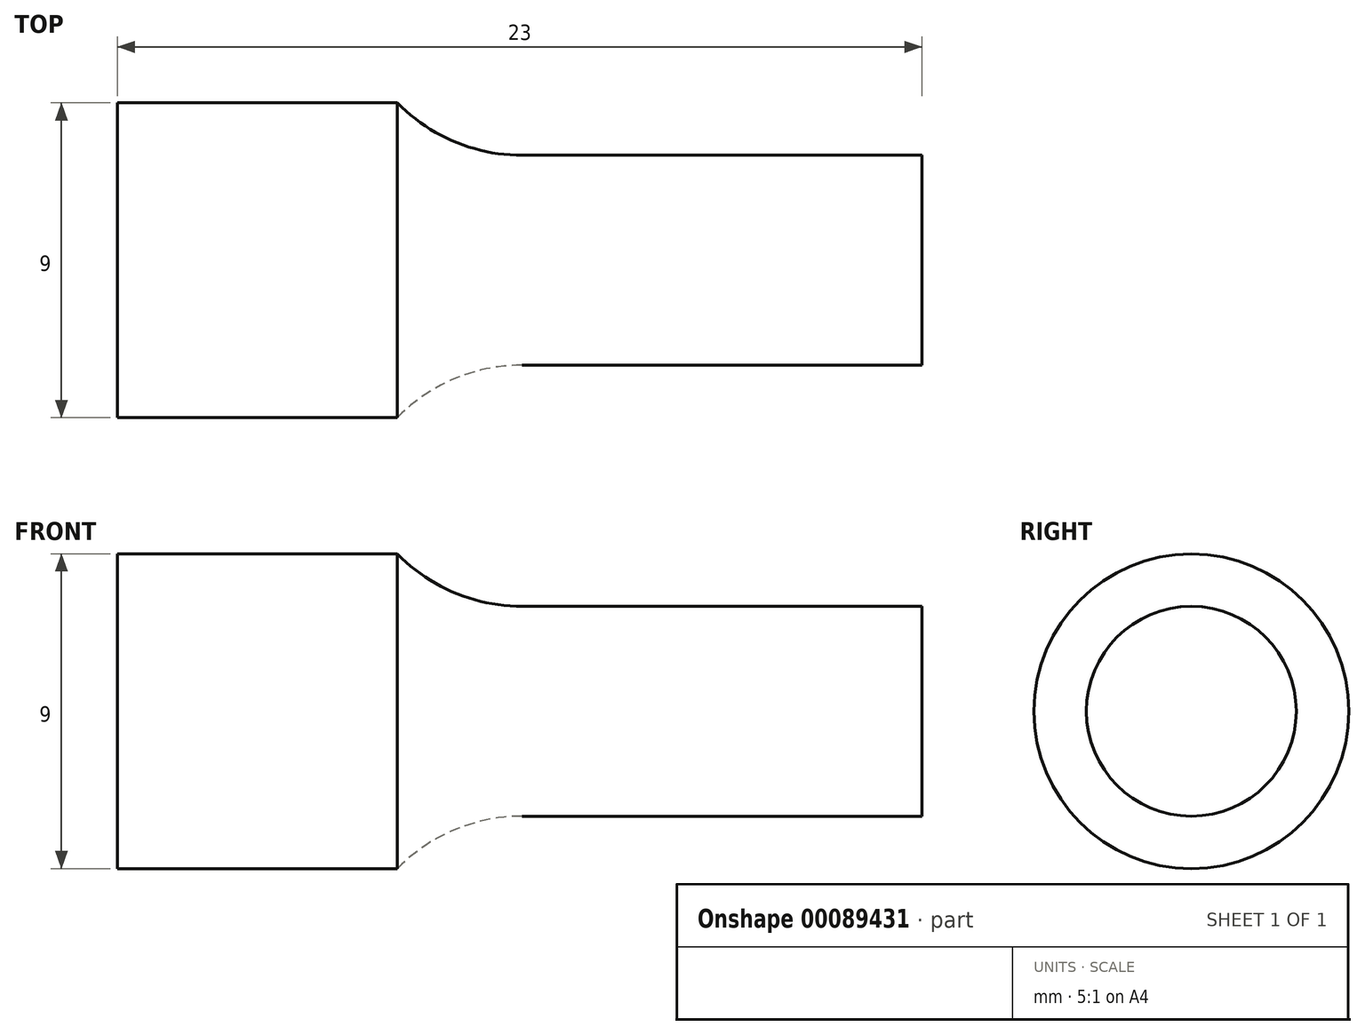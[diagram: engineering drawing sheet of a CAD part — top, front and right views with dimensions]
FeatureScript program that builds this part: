
annotation { "Feature Type Name" : "Feature", "Feature Type Description" : "" }
export const myFeature = defineFeature(function(context is Context, id is Id, definition is map)
    precondition{}
    {
        {
            var Q0;
            Q0=qCreatedBy(makeId("Top.planeOp"),FACE);
            var sketch = newSketch(context, id + "F0", { "sketchPlane" : qUnion([Q0])});
            skLineSegment(sketch, "E0", {"start": v(-11.5, 0) * mm, "end": v(-11.5, 4.5) * mm});
            skLineSegment(sketch, "E1", {"start": v(-11.5, 4.5) * mm, "end": v(-3.5, 4.5) * mm});
            skLineSegment(sketch, "E2", {"start": v(-3.5, 4.5) * mm, "end": v(-3.5, 3) * mm});
            skLineSegment(sketch, "E3", {"start": v(-3.5, 3) * mm, "end": v(11.5, 3) * mm});
            skLineSegment(sketch, "E4", {"start": v(11.5, 3) * mm, "end": v(11.5, 0) * mm});
            skLineSegment(sketch, "E5", {"start": v(11.5, 0) * mm, "end": v(-11.5, 0) * mm});
            skLineSegment(sketch, "E6", {"start": v(-37.65, 0) * mm, "end": v(31.92, 0) * mm, "construction": true});
            skSolve(sketch);
        }
        {
            var Q0;
            Q0=makeQuery(id+"F0.imprint","IMPRINT",FACE,{"disambiguationData":[TD([[makeQuery(id+"F0.imprint","IMPRINT",EDGE,{"derivedFrom":sQuery(id+"F0.wireOp",EDGE,"E0")}),-1.0]])]});
            var Q1;
            Q1=sQuery(id+"F0.wireOp",EDGE,"E6");
            revolve(context, id + "F1", {"entities" : qUnion([Q0]), "axis" : qUnion([Q1]), "revolveType" : RevolveType.FULL});
        }
        {
            var Q0;
            Q0=makeQuery(id+"F1.opRevolve","SWEPT_EDGE",EDGE,{"disambiguationData":[OSD([sQuery(id+"F0.wireOp",EDGE,"E2"),sQuery(id+"F0.wireOp",EDGE,"E3")])]});
            fillet(context, id + "F2", {"entities" : qUnion([Q0]), "radius" : 5 * mm, "tangentPropagation" : true, "allowEdgeOverflow" : false});
        }
    });
